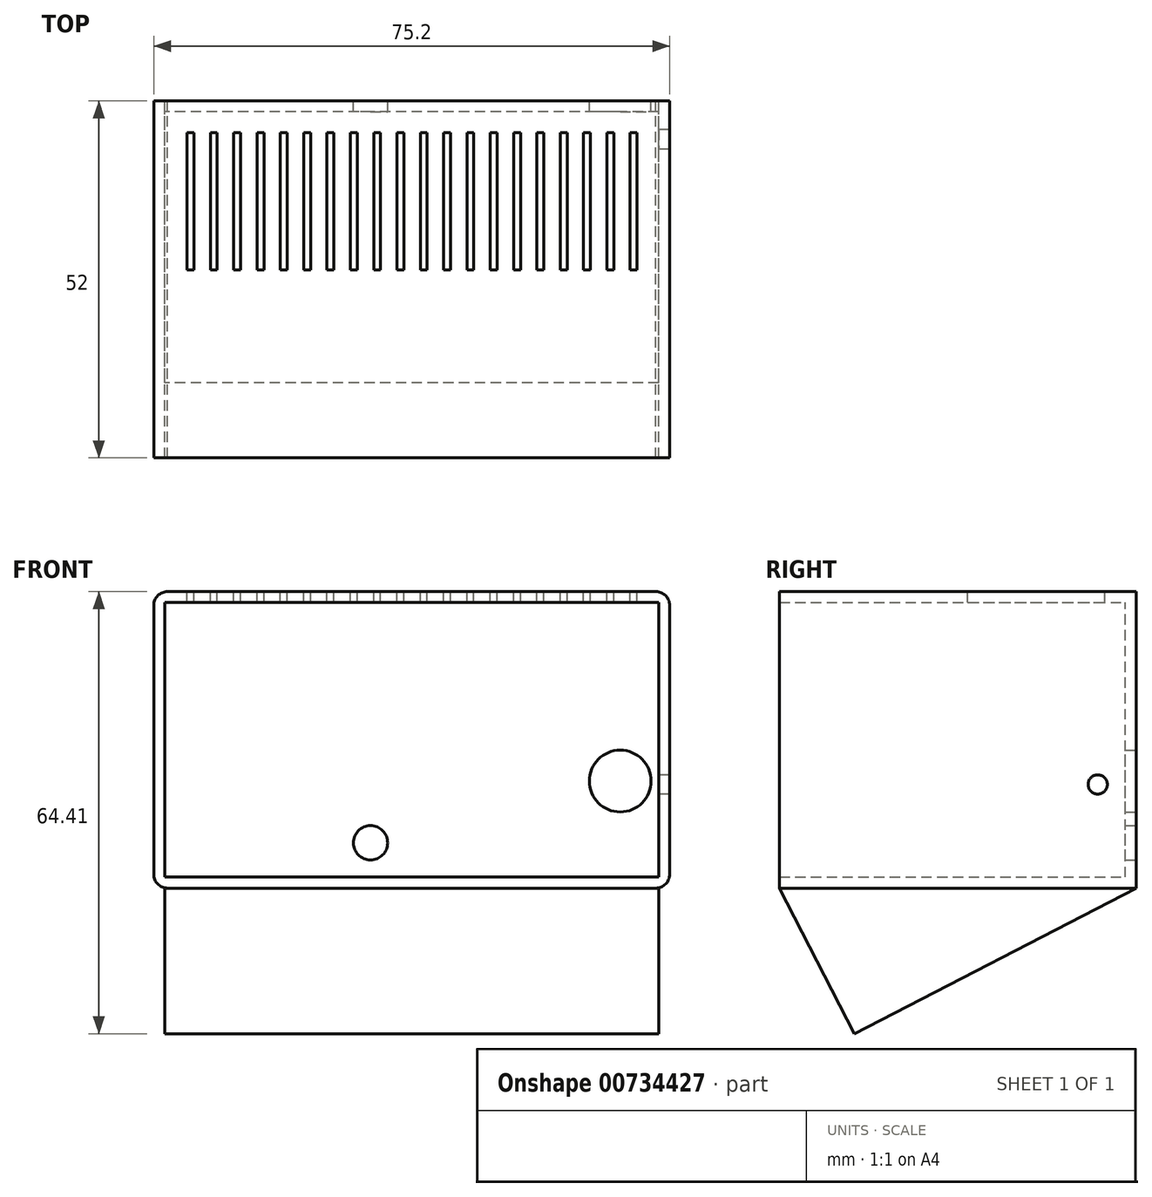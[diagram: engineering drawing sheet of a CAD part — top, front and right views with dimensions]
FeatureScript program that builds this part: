
annotation { "Feature Type Name" : "Feature", "Feature Type Description" : "" }
export const myFeature = defineFeature(function(context is Context, id is Id, definition is map)
    precondition{}
    {
        {
            var Q0;
            Q0=qCreatedBy(makeId("Front.planeOp"),FACE);
            var sketch = newSketch(context, id + "F0", { "sketchPlane" : qUnion([Q0])});
            skLineSegment(sketch, "E0.bottom", {"start": v(36, -20) * mm, "end": v(-36, -20) * mm});
            skLineSegment(sketch, "E0.top", {"start": v(36, 20) * mm, "end": v(-36, 20) * mm});
            skLineSegment(sketch, "E0.left", {"start": v(36, -20) * mm, "end": v(36, 20) * mm});
            skLineSegment(sketch, "E0.right", {"start": v(-36, -20) * mm, "end": v(-36, 20) * mm});
            skPoint(sketch, "E0.middle", {"position": v(0, 0) * mm});
            skLineSegment(sketch, "E1.0", {"start": v(-37.6, -21.6) * mm, "end": v(-37.6, 21.6) * mm});
            skLineSegment(sketch, "E1.1", {"start": v(37.6, -21.6) * mm, "end": v(-37.6, -21.6) * mm});
            skLineSegment(sketch, "E1.2", {"start": v(37.6, -21.6) * mm, "end": v(37.6, 21.6) * mm});
            skLineSegment(sketch, "E1.3", {"start": v(37.6, 21.6) * mm, "end": v(-37.6, 21.6) * mm});
            skPoint(sketch, "E2", {"position": v(30.4, -6) * mm});
            skPoint(sketch, "E3", {"position": v(-6, -15) * mm});
            skSolve(sketch);
        }
        {
            var Q0;
            Q0=makeQuery(id+"F0.imprint","IMPRINT",FACE,{"disambiguationData":[TD([[makeQuery(id+"F0.imprint","IMPRINT",EDGE,{"derivedFrom":sQuery(id+"F0.wireOp",EDGE,"E0.bottom")}),1.0]])]});
            extrude(context, id + "F1", {"entities" : qUnion([Q0]), "depth" : 52 * mm, "offsetDistance" : 25 * mm});
        }
        {
            var Q0;
            Q0=makeQuery(id+"F1.opExtrude","SWEPT_EDGE",EDGE,{"disambiguationData":[OSD([sQuery(id+"F0.wireOp",EDGE,"E1.2"),sQuery(id+"F0.wireOp",EDGE,"E1.3")])]});
            var Q1;
            Q1=makeQuery(id+"F1.opExtrude","SWEPT_EDGE",EDGE,{"disambiguationData":[OSD([sQuery(id+"F0.wireOp",EDGE,"E1.0"),sQuery(id+"F0.wireOp",EDGE,"E1.3")])]});
            var Q2;
            Q2=makeQuery(id+"F1.opExtrude","SWEPT_EDGE",EDGE,{"disambiguationData":[OSD([sQuery(id+"F0.wireOp",EDGE,"E1.0"),sQuery(id+"F0.wireOp",EDGE,"E1.1")])]});
            var Q3;
            Q3=makeQuery(id+"F1.opExtrude","SWEPT_EDGE",EDGE,{"disambiguationData":[OSD([sQuery(id+"F0.wireOp",EDGE,"E1.1"),sQuery(id+"F0.wireOp",EDGE,"E1.2")])]});
            fillet(context, id + "F2", {"entities" : qUnion([Q0, Q1, Q2, Q3]), "radius" : 2 * mm, "tangentPropagation" : true, "allowEdgeOverflow" : false});
        }
        {
            var Q0;
            Q0=makeQuery(id+"F0.imprint","IMPRINT",FACE,{"disambiguationData":[TD([[makeQuery(id+"F0.imprint","IMPRINT",EDGE,{"derivedFrom":sQuery(id+"F0.wireOp",EDGE,"E0.bottom")}),-1.0]])]});
            extrude(context, id + "F3", {"entities" : qUnion([Q0]), "operationType" : NewBodyOperationType.ADD, "depth" : 1.6 * mm, "offsetDistance" : 25 * mm});
        }
        {
            var Q0;
            Q0=qCreatedBy(makeId("Right.planeOp"),FACE);
            var sketch = newSketch(context, id + "F4", { "sketchPlane" : qUnion([Q0])});
            skPoint(sketch, "E4.0", {"position": v(-52, -21.6) * mm});
            skLineSegment(sketch, "E5", {"start": v(-52, -21.6) * mm, "end": v(-41.04, -42.8) * mm});
            skLineSegment(sketch, "E6", {"start": v(-41.04, -42.8) * mm, "end": v(0, -21.6) * mm});
            skLineSegment(sketch, "E7", {"start": v(-52, -21.6) * mm, "end": v(0, -21.6) * mm});
            skSolve(sketch);
        }
        {
            var Q0;
            Q0=makeQuery(id+"F4.imprint","IMPRINT",FACE,{"disambiguationData":[TD([[makeQuery(id+"F4.imprint","IMPRINT",EDGE,{"derivedFrom":sQuery(id+"F4.wireOp",EDGE,"E5")}),1.0]])]});
            extrude(context, id + "F5", {"entities" : qUnion([Q0]), "operationType" : NewBodyOperationType.ADD, "endBound" : BoundingType.SYMMETRIC, "depth" : 72 * mm, "offsetDistance" : 25 * mm});
        }
        {
            var Q0;
            Q0=sQuery(id+"F0.wireOp",VERTEX,"E2");
            var Q1;
            Q1=makeQuery(id+"F1.opExtrude","SWEPT_BODY",BODY,{"disambiguationData":[OSD([sQuery(id+"F0.wireOp",EDGE,"E0.bottom"),sQuery(id+"F0.wireOp",EDGE,"E0.top"),sQuery(id+"F0.wireOp",EDGE,"E0.left"),sQuery(id+"F0.wireOp",EDGE,"E0.right"),sQuery(id+"F0.wireOp",EDGE,"E1.0"),sQuery(id+"F0.wireOp",EDGE,"E1.1"),sQuery(id+"F0.wireOp",EDGE,"E1.2"),sQuery(id+"F0.wireOp",EDGE,"E1.3")])]});
            hole(context, id + "F6", {"style" : HoleStyle.SIMPLE, "endStyle" : HoleEndStyle.THROUGH, "oppositeDirection" : true, "holeDiameter" : 9 * mm, "majorDiameter" : 5 * mm, "isTappedThrough" : true, "tappedDepth" : 12 * mm, "tapClearance" : 3, "locations" : qUnion([Q0]), "scope" : qUnion([Q1])});
        }
        {
            var Q0;
            Q0=makeQuery(id+"F1.opExtrude","SWEPT_FACE",FACE,{"disambiguationData":[OSD([sQuery(id+"F0.wireOp",EDGE,"E0.left")])]});
            var sketch = newSketch(context, id + "F7", { "sketchPlane" : qUnion([Q0])});
            skPoint(sketch, "E8", {"position": v(5.6, -6.5) * mm});
            skSolve(sketch);
        }
        {
            var Q0;
            Q0=sQuery(id+"F7.wireOp",VERTEX,"E8");
            var Q1;
            Q1=makeQuery(id+"F1.opExtrude","SWEPT_BODY",BODY,{"disambiguationData":[OSD([sQuery(id+"F0.wireOp",EDGE,"E0.bottom"),sQuery(id+"F0.wireOp",EDGE,"E0.top"),sQuery(id+"F0.wireOp",EDGE,"E0.left"),sQuery(id+"F0.wireOp",EDGE,"E0.right"),sQuery(id+"F0.wireOp",EDGE,"E1.0"),sQuery(id+"F0.wireOp",EDGE,"E1.1"),sQuery(id+"F0.wireOp",EDGE,"E1.2"),sQuery(id+"F0.wireOp",EDGE,"E1.3")])]});
            hole(context, id + "F8", {"style" : HoleStyle.SIMPLE, "endStyle" : HoleEndStyle.THROUGH, "holeDiameter" : 2.8 * mm, "majorDiameter" : 5 * mm, "isTappedThrough" : true, "tappedDepth" : 12 * mm, "tapClearance" : 3, "locations" : qUnion([Q0]), "scope" : qUnion([Q1])});
        }
        {
            var Q0;
            Q0=sQuery(id+"F0.wireOp",VERTEX,"E3");
            var Q1;
            Q1=makeQuery(id+"F1.opExtrude","SWEPT_BODY",BODY,{"disambiguationData":[OSD([sQuery(id+"F0.wireOp",EDGE,"E0.bottom"),sQuery(id+"F0.wireOp",EDGE,"E0.top"),sQuery(id+"F0.wireOp",EDGE,"E0.left"),sQuery(id+"F0.wireOp",EDGE,"E0.right"),sQuery(id+"F0.wireOp",EDGE,"E1.0"),sQuery(id+"F0.wireOp",EDGE,"E1.1"),sQuery(id+"F0.wireOp",EDGE,"E1.2"),sQuery(id+"F0.wireOp",EDGE,"E1.3")])]});
            hole(context, id + "F9", {"style" : HoleStyle.SIMPLE, "endStyle" : HoleEndStyle.THROUGH, "oppositeDirection" : true, "holeDiameter" : 5 * mm, "majorDiameter" : 5 * mm, "isTappedThrough" : true, "tappedDepth" : 12 * mm, "tapClearance" : 3, "locations" : qUnion([Q0]), "scope" : qUnion([Q1])});
        }
        {
            var Q0;
            Q0=makeQuery(id+"F1.opExtrude","SWEPT_FACE",FACE,{"disambiguationData":[OSD([sQuery(id+"F0.wireOp",EDGE,"E1.3")])]});
            var sketch = newSketch(context, id + "F10", { "sketchPlane" : qUnion([Q0])});
            skLineSegment(sketch, "E9.bottom", {"start": v(-32.74, -4.6) * mm, "end": v(-31.74, -4.6) * mm});
            skLineSegment(sketch, "E9.top", {"start": v(-32.74, -24.6) * mm, "end": v(-31.74, -24.6) * mm});
            skLineSegment(sketch, "E9.left", {"start": v(-32.74, -4.6) * mm, "end": v(-32.74, -24.6) * mm});
            skLineSegment(sketch, "E9.right", {"start": v(-31.74, -4.6) * mm, "end": v(-31.74, -24.6) * mm});
            skLineSegment(sketch, "E10.1.0.0", {"start": v(-29.34, -4.6) * mm, "end": v(-28.34, -4.6) * mm});
            skLineSegment(sketch, "E10.1.0.1", {"start": v(-29.34, -4.6) * mm, "end": v(-29.34, -24.6) * mm});
            skLineSegment(sketch, "E10.1.0.2", {"start": v(-28.34, -4.6) * mm, "end": v(-28.34, -24.6) * mm});
            skLineSegment(sketch, "E10.1.0.3", {"start": v(-29.34, -24.6) * mm, "end": v(-28.34, -24.6) * mm});
            skLineSegment(sketch, "E10.2.0.0", {"start": v(-25.94, -4.6) * mm, "end": v(-24.94, -4.6) * mm});
            skLineSegment(sketch, "E10.2.0.1", {"start": v(-25.94, -4.6) * mm, "end": v(-25.94, -24.6) * mm});
            skLineSegment(sketch, "E10.2.0.2", {"start": v(-24.94, -4.6) * mm, "end": v(-24.94, -24.6) * mm});
            skLineSegment(sketch, "E10.2.0.3", {"start": v(-25.94, -24.6) * mm, "end": v(-24.94, -24.6) * mm});
            skLineSegment(sketch, "E10.3.0.0", {"start": v(-22.54, -4.6) * mm, "end": v(-21.54, -4.6) * mm});
            skLineSegment(sketch, "E10.3.0.1", {"start": v(-22.54, -4.6) * mm, "end": v(-22.54, -24.6) * mm});
            skLineSegment(sketch, "E10.3.0.2", {"start": v(-21.54, -4.6) * mm, "end": v(-21.54, -24.6) * mm});
            skLineSegment(sketch, "E10.3.0.3", {"start": v(-22.54, -24.6) * mm, "end": v(-21.54, -24.6) * mm});
            skLineSegment(sketch, "E10.4.0.0", {"start": v(-19.14, -4.6) * mm, "end": v(-18.14, -4.6) * mm});
            skLineSegment(sketch, "E10.4.0.1", {"start": v(-19.14, -4.6) * mm, "end": v(-19.14, -24.6) * mm});
            skLineSegment(sketch, "E10.4.0.2", {"start": v(-18.14, -4.6) * mm, "end": v(-18.14, -24.6) * mm});
            skLineSegment(sketch, "E10.4.0.3", {"start": v(-19.14, -24.6) * mm, "end": v(-18.14, -24.6) * mm});
            skLineSegment(sketch, "E10.5.0.0", {"start": v(-15.74, -4.6) * mm, "end": v(-14.74, -4.6) * mm});
            skLineSegment(sketch, "E10.5.0.1", {"start": v(-15.74, -4.6) * mm, "end": v(-15.74, -24.6) * mm});
            skLineSegment(sketch, "E10.5.0.2", {"start": v(-14.74, -4.6) * mm, "end": v(-14.74, -24.6) * mm});
            skLineSegment(sketch, "E10.5.0.3", {"start": v(-15.74, -24.6) * mm, "end": v(-14.74, -24.6) * mm});
            skLineSegment(sketch, "E10.6.0.0", {"start": v(-12.34, -4.6) * mm, "end": v(-11.34, -4.6) * mm});
            skLineSegment(sketch, "E10.6.0.1", {"start": v(-12.34, -4.6) * mm, "end": v(-12.34, -24.6) * mm});
            skLineSegment(sketch, "E10.6.0.2", {"start": v(-11.34, -4.6) * mm, "end": v(-11.34, -24.6) * mm});
            skLineSegment(sketch, "E10.6.0.3", {"start": v(-12.34, -24.6) * mm, "end": v(-11.34, -24.6) * mm});
            skLineSegment(sketch, "E10.7.0.0", {"start": v(-8.94, -4.6) * mm, "end": v(-7.94, -4.6) * mm});
            skLineSegment(sketch, "E10.7.0.1", {"start": v(-8.94, -4.6) * mm, "end": v(-8.94, -24.6) * mm});
            skLineSegment(sketch, "E10.7.0.2", {"start": v(-7.94, -4.6) * mm, "end": v(-7.94, -24.6) * mm});
            skLineSegment(sketch, "E10.7.0.3", {"start": v(-8.94, -24.6) * mm, "end": v(-7.94, -24.6) * mm});
            skLineSegment(sketch, "E10.8.0.0", {"start": v(-5.54, -4.6) * mm, "end": v(-4.54, -4.6) * mm});
            skLineSegment(sketch, "E10.8.0.1", {"start": v(-5.54, -4.6) * mm, "end": v(-5.54, -24.6) * mm});
            skLineSegment(sketch, "E10.8.0.2", {"start": v(-4.54, -4.6) * mm, "end": v(-4.54, -24.6) * mm});
            skLineSegment(sketch, "E10.8.0.3", {"start": v(-5.54, -24.6) * mm, "end": v(-4.54, -24.6) * mm});
            skLineSegment(sketch, "E10.9.0.0", {"start": v(-2.14, -4.6) * mm, "end": v(-1.14, -4.6) * mm});
            skLineSegment(sketch, "E10.9.0.1", {"start": v(-2.14, -4.6) * mm, "end": v(-2.14, -24.6) * mm});
            skLineSegment(sketch, "E10.9.0.2", {"start": v(-1.14, -4.6) * mm, "end": v(-1.14, -24.6) * mm});
            skLineSegment(sketch, "E10.9.0.3", {"start": v(-2.14, -24.6) * mm, "end": v(-1.14, -24.6) * mm});
            skLineSegment(sketch, "E10.10.0.0", {"start": v(1.26, -4.6) * mm, "end": v(2.26, -4.6) * mm});
            skLineSegment(sketch, "E10.10.0.1", {"start": v(1.26, -4.6) * mm, "end": v(1.26, -24.6) * mm});
            skLineSegment(sketch, "E10.10.0.2", {"start": v(2.26, -4.6) * mm, "end": v(2.26, -24.6) * mm});
            skLineSegment(sketch, "E10.10.0.3", {"start": v(1.26, -24.6) * mm, "end": v(2.26, -24.6) * mm});
            skLineSegment(sketch, "E10.11.0.0", {"start": v(4.66, -4.6) * mm, "end": v(5.66, -4.6) * mm});
            skLineSegment(sketch, "E10.11.0.1", {"start": v(4.66, -4.6) * mm, "end": v(4.66, -24.6) * mm});
            skLineSegment(sketch, "E10.11.0.2", {"start": v(5.66, -4.6) * mm, "end": v(5.66, -24.6) * mm});
            skLineSegment(sketch, "E10.11.0.3", {"start": v(4.66, -24.6) * mm, "end": v(5.66, -24.6) * mm});
            skLineSegment(sketch, "E10.12.0.0", {"start": v(8.06, -4.6) * mm, "end": v(9.06, -4.6) * mm});
            skLineSegment(sketch, "E10.12.0.1", {"start": v(8.06, -4.6) * mm, "end": v(8.06, -24.6) * mm});
            skLineSegment(sketch, "E10.12.0.2", {"start": v(9.06, -4.6) * mm, "end": v(9.06, -24.6) * mm});
            skLineSegment(sketch, "E10.12.0.3", {"start": v(8.06, -24.6) * mm, "end": v(9.06, -24.6) * mm});
            skLineSegment(sketch, "E10.13.0.0", {"start": v(11.46, -4.6) * mm, "end": v(12.46, -4.6) * mm});
            skLineSegment(sketch, "E10.13.0.1", {"start": v(11.46, -4.6) * mm, "end": v(11.46, -24.6) * mm});
            skLineSegment(sketch, "E10.13.0.2", {"start": v(12.46, -4.6) * mm, "end": v(12.46, -24.6) * mm});
            skLineSegment(sketch, "E10.13.0.3", {"start": v(11.46, -24.6) * mm, "end": v(12.46, -24.6) * mm});
            skLineSegment(sketch, "E10.14.0.0", {"start": v(14.86, -4.6) * mm, "end": v(15.86, -4.6) * mm});
            skLineSegment(sketch, "E10.14.0.1", {"start": v(14.86, -4.6) * mm, "end": v(14.86, -24.6) * mm});
            skLineSegment(sketch, "E10.14.0.2", {"start": v(15.86, -4.6) * mm, "end": v(15.86, -24.6) * mm});
            skLineSegment(sketch, "E10.14.0.3", {"start": v(14.86, -24.6) * mm, "end": v(15.86, -24.6) * mm});
            skLineSegment(sketch, "E10.15.0.0", {"start": v(18.26, -4.6) * mm, "end": v(19.26, -4.6) * mm});
            skLineSegment(sketch, "E10.15.0.1", {"start": v(18.26, -4.6) * mm, "end": v(18.26, -24.6) * mm});
            skLineSegment(sketch, "E10.15.0.2", {"start": v(19.26, -4.6) * mm, "end": v(19.26, -24.6) * mm});
            skLineSegment(sketch, "E10.15.0.3", {"start": v(18.26, -24.6) * mm, "end": v(19.26, -24.6) * mm});
            skLineSegment(sketch, "E10.16.0.0", {"start": v(21.66, -4.6) * mm, "end": v(22.66, -4.6) * mm});
            skLineSegment(sketch, "E10.16.0.1", {"start": v(21.66, -4.6) * mm, "end": v(21.66, -24.6) * mm});
            skLineSegment(sketch, "E10.16.0.2", {"start": v(22.66, -4.6) * mm, "end": v(22.66, -24.6) * mm});
            skLineSegment(sketch, "E10.16.0.3", {"start": v(21.66, -24.6) * mm, "end": v(22.66, -24.6) * mm});
            skLineSegment(sketch, "E10.17.0.0", {"start": v(25.06, -4.6) * mm, "end": v(26.06, -4.6) * mm});
            skLineSegment(sketch, "E10.17.0.1", {"start": v(25.06, -4.6) * mm, "end": v(25.06, -24.6) * mm});
            skLineSegment(sketch, "E10.17.0.2", {"start": v(26.06, -4.6) * mm, "end": v(26.06, -24.6) * mm});
            skLineSegment(sketch, "E10.17.0.3", {"start": v(25.06, -24.6) * mm, "end": v(26.06, -24.6) * mm});
            skLineSegment(sketch, "E10.18.0.0", {"start": v(28.46, -4.6) * mm, "end": v(29.46, -4.6) * mm});
            skLineSegment(sketch, "E10.18.0.1", {"start": v(28.46, -4.6) * mm, "end": v(28.46, -24.6) * mm});
            skLineSegment(sketch, "E10.18.0.2", {"start": v(29.46, -4.6) * mm, "end": v(29.46, -24.6) * mm});
            skLineSegment(sketch, "E10.18.0.3", {"start": v(28.46, -24.6) * mm, "end": v(29.46, -24.6) * mm});
            skLineSegment(sketch, "E10.19.0.0", {"start": v(31.86, -4.6) * mm, "end": v(32.86, -4.6) * mm});
            skLineSegment(sketch, "E10.19.0.1", {"start": v(31.86, -4.6) * mm, "end": v(31.86, -24.6) * mm});
            skLineSegment(sketch, "E10.19.0.2", {"start": v(32.86, -4.6) * mm, "end": v(32.86, -24.6) * mm});
            skLineSegment(sketch, "E10.19.0.3", {"start": v(31.86, -24.6) * mm, "end": v(32.86, -24.6) * mm});
            skLineSegment(sketch, "E10.direction1", {"start": v(-32.74, -4.6) * mm, "end": v(-29.34, -4.6) * mm, "construction": true});
            skSolve(sketch);
        }
        {
            var Q0;
            Q0=makeQuery(id+"F10.imprint","IMPRINT",FACE,{"disambiguationData":[TD([[makeQuery(id+"F10.imprint","IMPRINT",EDGE,{"derivedFrom":sQuery(id+"F10.wireOp",EDGE,"E9.bottom")}),-1.0]])]});
            var Q1;
            Q1=makeQuery(id+"F10.imprint","IMPRINT",FACE,{"disambiguationData":[TD([[makeQuery(id+"F10.imprint","IMPRINT",EDGE,{"derivedFrom":sQuery(id+"F10.wireOp",EDGE,"E10.1.0.0")}),-1.0]])]});
            var Q2;
            Q2=makeQuery(id+"F10.imprint","IMPRINT",FACE,{"disambiguationData":[TD([[makeQuery(id+"F10.imprint","IMPRINT",EDGE,{"derivedFrom":sQuery(id+"F10.wireOp",EDGE,"E10.2.0.0")}),-1.0]])]});
            var Q3;
            Q3=makeQuery(id+"F10.imprint","IMPRINT",FACE,{"disambiguationData":[TD([[makeQuery(id+"F10.imprint","IMPRINT",EDGE,{"derivedFrom":sQuery(id+"F10.wireOp",EDGE,"E10.3.0.0")}),-1.0]])]});
            var Q4;
            Q4=makeQuery(id+"F10.imprint","IMPRINT",FACE,{"disambiguationData":[TD([[makeQuery(id+"F10.imprint","IMPRINT",EDGE,{"derivedFrom":sQuery(id+"F10.wireOp",EDGE,"E10.4.0.0")}),-1.0]])]});
            var Q5;
            Q5=makeQuery(id+"F10.imprint","IMPRINT",FACE,{"disambiguationData":[TD([[makeQuery(id+"F10.imprint","IMPRINT",EDGE,{"derivedFrom":sQuery(id+"F10.wireOp",EDGE,"E10.5.0.0")}),-1.0]])]});
            var Q6;
            Q6=makeQuery(id+"F10.imprint","IMPRINT",FACE,{"disambiguationData":[TD([[makeQuery(id+"F10.imprint","IMPRINT",EDGE,{"derivedFrom":sQuery(id+"F10.wireOp",EDGE,"E10.6.0.0")}),-1.0]])]});
            var Q7;
            Q7=makeQuery(id+"F10.imprint","IMPRINT",FACE,{"disambiguationData":[TD([[makeQuery(id+"F10.imprint","IMPRINT",EDGE,{"derivedFrom":sQuery(id+"F10.wireOp",EDGE,"E10.7.0.0")}),-1.0]])]});
            var Q8;
            Q8=makeQuery(id+"F10.imprint","IMPRINT",FACE,{"disambiguationData":[TD([[makeQuery(id+"F10.imprint","IMPRINT",EDGE,{"derivedFrom":sQuery(id+"F10.wireOp",EDGE,"E10.8.0.0")}),-1.0]])]});
            var Q9;
            Q9=makeQuery(id+"F10.imprint","IMPRINT",FACE,{"disambiguationData":[TD([[makeQuery(id+"F10.imprint","IMPRINT",EDGE,{"derivedFrom":sQuery(id+"F10.wireOp",EDGE,"E10.10.0.0")}),-1.0]])]});
            var Q10;
            Q10=makeQuery(id+"F10.imprint","IMPRINT",FACE,{"disambiguationData":[TD([[makeQuery(id+"F10.imprint","IMPRINT",EDGE,{"derivedFrom":sQuery(id+"F10.wireOp",EDGE,"E10.11.0.0")}),-1.0]])]});
            var Q11;
            Q11=makeQuery(id+"F10.imprint","IMPRINT",FACE,{"disambiguationData":[TD([[makeQuery(id+"F10.imprint","IMPRINT",EDGE,{"derivedFrom":sQuery(id+"F10.wireOp",EDGE,"E10.9.0.0")}),-1.0]])]});
            var Q12;
            Q12=makeQuery(id+"F10.imprint","IMPRINT",FACE,{"disambiguationData":[TD([[makeQuery(id+"F10.imprint","IMPRINT",EDGE,{"derivedFrom":sQuery(id+"F10.wireOp",EDGE,"E10.12.0.0")}),-1.0]])]});
            var Q13;
            Q13=makeQuery(id+"F10.imprint","IMPRINT",FACE,{"disambiguationData":[TD([[makeQuery(id+"F10.imprint","IMPRINT",EDGE,{"derivedFrom":sQuery(id+"F10.wireOp",EDGE,"E10.13.0.0")}),-1.0]])]});
            var Q14;
            Q14=makeQuery(id+"F10.imprint","IMPRINT",FACE,{"disambiguationData":[TD([[makeQuery(id+"F10.imprint","IMPRINT",EDGE,{"derivedFrom":sQuery(id+"F10.wireOp",EDGE,"E10.14.0.0")}),-1.0]])]});
            var Q15;
            Q15=makeQuery(id+"F10.imprint","IMPRINT",FACE,{"disambiguationData":[TD([[makeQuery(id+"F10.imprint","IMPRINT",EDGE,{"derivedFrom":sQuery(id+"F10.wireOp",EDGE,"E10.15.0.0")}),-1.0]])]});
            var Q16;
            Q16=makeQuery(id+"F10.imprint","IMPRINT",FACE,{"disambiguationData":[TD([[makeQuery(id+"F10.imprint","IMPRINT",EDGE,{"derivedFrom":sQuery(id+"F10.wireOp",EDGE,"E10.16.0.0")}),-1.0]])]});
            var Q17;
            Q17=makeQuery(id+"F10.imprint","IMPRINT",FACE,{"disambiguationData":[TD([[makeQuery(id+"F10.imprint","IMPRINT",EDGE,{"derivedFrom":sQuery(id+"F10.wireOp",EDGE,"E10.17.0.0")}),-1.0]])]});
            var Q18;
            Q18=makeQuery(id+"F10.imprint","IMPRINT",FACE,{"disambiguationData":[TD([[makeQuery(id+"F10.imprint","IMPRINT",EDGE,{"derivedFrom":sQuery(id+"F10.wireOp",EDGE,"E10.18.0.0")}),-1.0]])]});
            var Q19;
            Q19=makeQuery(id+"F10.imprint","IMPRINT",FACE,{"disambiguationData":[TD([[makeQuery(id+"F10.imprint","IMPRINT",EDGE,{"derivedFrom":sQuery(id+"F10.wireOp",EDGE,"E10.19.0.0")}),-1.0]])]});
            extrude(context, id + "F11", {"entities" : qUnion([Q0, Q1, Q2, Q3, Q4, Q5, Q6, Q7, Q8, Q9, Q10, Q11, Q12, Q13, Q14, Q15, Q16, Q17, Q18, Q19]), "operationType" : NewBodyOperationType.REMOVE, "oppositeDirection" : true, "depth" : 25 * mm, "offsetDistance" : 25 * mm});
        }
    });
